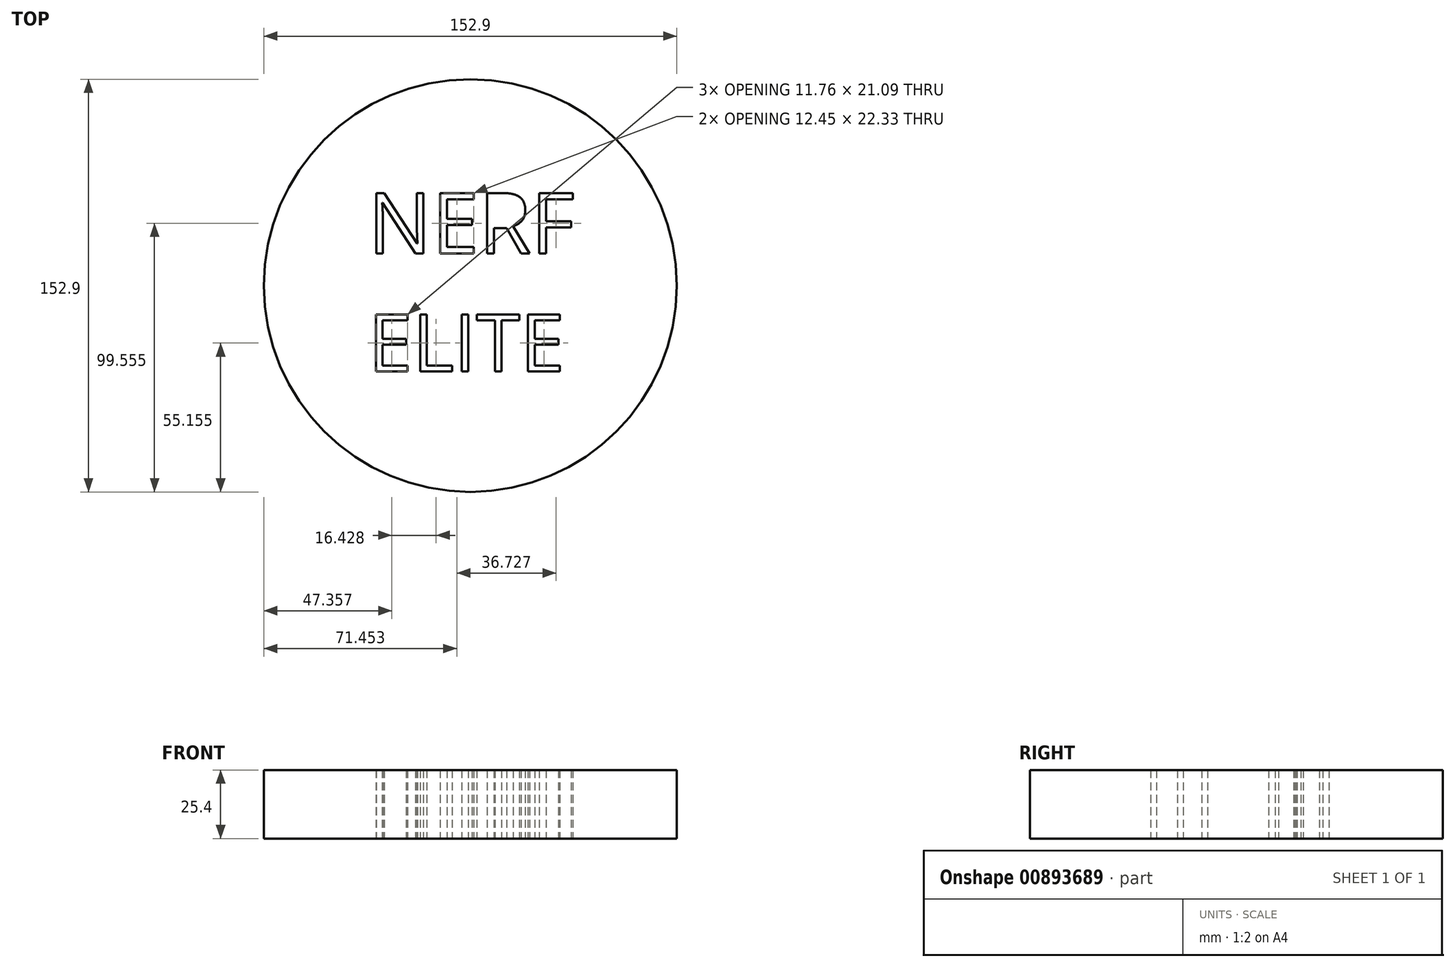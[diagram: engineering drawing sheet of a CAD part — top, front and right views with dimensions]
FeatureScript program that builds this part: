
annotation { "Feature Type Name" : "Feature", "Feature Type Description" : "" }
export const myFeature = defineFeature(function(context is Context, id is Id, definition is map)
    precondition{}
    {
        {
            var Q0;
            Q0=qCreatedBy(makeId("Top.planeOp"),FACE);
            var sketch = newSketch(context, id + "F0", { "sketchPlane" : qUnion([Q0])});
            skCircle(sketch, "E0", {"center": v(0, 0) * mm, "radius": 76.45 * mm});
            skPoint(sketch, "E1.start.orphan", {"position": v(-19, 61) * mm});
            skPoint(sketch, "E2.end.orphan", {"position": v(0, 66.3) * mm});
            skPoint(sketch, "E3.orphan", {"position": v(-6.7, 66.3) * mm});
            skPoint(sketch, "E4.orphan", {"position": v(-6.7, 61.38) * mm});
            skPoint(sketch, "E5.end.orphan", {"position": v(0, 55.7) * mm});
            skPoint(sketch, "E6.start.orphan", {"position": v(0, 61.38) * mm});
            skPoint(sketch, "E7.start.orphan", {"position": v(7.77, 66.3) * mm});
            skPoint(sketch, "E8.end.orphan", {"position": v(7.77, 55.7) * mm});
            skPoint(sketch, "E8.start.orphan", {"position": v(7.77, 61.38) * mm});
            skLineSegment(sketch, "E9", {"start": v(2.86, 56.23) * mm, "end": v(2.87, 56.23) * mm});
            skPoint(sketch, "E10.start.orphan", {"position": v(-1.19, 62.03) * mm});
            skText(sketch, "E11", { "text": "NERF\n", "fontName": "OpenSans-Regular.ttf"});
            skPoint(sketch, "E12.start.orphan", {"position": v(-30.54, 66.3) * mm});
            skPoint(sketch, "E13.start.orphan", {"position": v(-30.54, 68.75) * mm});
            skPoint(sketch, "E14.end.orphan", {"position": v(-24.08, 66.3) * mm});
            skPoint(sketch, "E15.start.orphan", {"position": v(-21.53, 68.75) * mm});
            skPoint(sketch, "E16.start.orphan", {"position": v(-13.15, 68.75) * mm});
            skPoint(sketch, "E17.end.orphan", {"position": v(-13.15, 66.3) * mm});
            skPoint(sketch, "E18.end.orphan", {"position": v(-19, 66.3) * mm});
            skPoint(sketch, "E19.end.orphan", {"position": v(-19, 61.65) * mm});
            skPoint(sketch, "E20.start.orphan", {"position": v(-19, 55.7) * mm});
            skPoint(sketch, "E21.start.orphan", {"position": v(-13.15, 55.7) * mm});
            skPoint(sketch, "E22.end.orphan", {"position": v(-1.12, 66.3) * mm});
            skPoint(sketch, "E23.end.orphan", {"position": v(-4.41, 64) * mm});
            skPoint(sketch, "E23.start.orphan", {"position": v(-4.41, 66.3) * mm});
            skPoint(sketch, "E24.end.orphan", {"position": v(1.65, 62.03) * mm});
            skPoint(sketch, "E25.end.orphan", {"position": v(-4.02, 55.7) * mm});
            skPoint(sketch, "E25.start.orphan", {"position": v(-4.02, 62.03) * mm});
            skPoint(sketch, "E26.end.orphan", {"position": v(-4.68, 55.7) * mm});
            skPoint(sketch, "E26.start.orphan", {"position": v(-6.7, 55.7) * mm});
            skPoint(sketch, "E27.end.orphan", {"position": v(9.81, 70.33) * mm});
            skPoint(sketch, "E28.start.orphan", {"position": v(17.58, 68.09) * mm});
            skPoint(sketch, "E29.start.orphan", {"position": v(13.9, 66.3) * mm});
            skPoint(sketch, "E30.end.orphan", {"position": v(17.58, 64) * mm});
            skPoint(sketch, "E31.end.orphan", {"position": v(17.58, 62.03) * mm});
            skPoint(sketch, "E32.end.orphan", {"position": v(13.9, 64.67) * mm});
            skPoint(sketch, "E33.end.orphan", {"position": v(13.9, 62.03) * mm});
            skPoint(sketch, "E34.end.orphan", {"position": v(13.9, 56.23) * mm});
            skPoint(sketch, "E34.start.orphan", {"position": v(9.81, 56.23) * mm});
            skLineSegment(sketch, "E35", {"start": v(-27.85, -42.67) * mm, "end": v(-27.85, -55.58) * mm});
            skLineSegment(sketch, "E36", {"start": v(-27.46, -55.58) * mm, "end": v(-22.06, -51.23) * mm});
            skLineSegment(sketch, "E37", {"start": v(-22.06, -51.23) * mm, "end": v(-22.06, -42.8) * mm});
            skLineSegment(sketch, "E38", {"start": v(-22.72, -42.8) * mm, "end": v(-27.85, -42.67) * mm});
            skLineSegment(sketch, "E39", {"start": v(-22.06, -51.23) * mm, "end": v(-15.5, -45.96) * mm});
            skLineSegment(sketch, "E40", {"start": v(-21.14, -42.8) * mm, "end": v(-18.37, -42.8) * mm});
            skLineSegment(sketch, "E41", {"start": v(-18.37, -42.54) * mm, "end": v(-18.37, -37.93) * mm});
            skLineSegment(sketch, "E42", {"start": v(-18.37, -37.93) * mm, "end": v(-12.05, -37.93) * mm});
            skArc(sketch, "E43", {"start": v(-8.89, -45.96) * mm, "mid": v(-12.2, -44.79) * mm, "end": v(-15.5, -45.96) * mm});
            skLineSegment(sketch, "E44", {"start": v(-8.89, -45.96) * mm, "end": v(-11.4, -52.68) * mm});
            skLineSegment(sketch, "E45", {"start": v(-11.4, -52.68) * mm, "end": v(-6.39, -52.68) * mm});
            skLineSegment(sketch, "E46", {"start": v(-6.39, -53.08) * mm, "end": v(-5.33, -45.96) * mm});
            skArc(sketch, "E47", {"start": v(1.25, -45.96) * mm, "mid": v(-2.04, -44.7) * mm, "end": v(-5.33, -45.96) * mm});
            skLineSegment(sketch, "E48", {"start": v(1.25, -45.96) * mm, "end": v(8.89, -45.96) * mm});
            skLineSegment(sketch, "E49", {"start": v(8.89, -45.96) * mm, "end": v(8.89, -61.9) * mm});
            skLineSegment(sketch, "E50", {"start": v(8.89, -61.9) * mm, "end": v(14.55, -61.9) * mm});
            skLineSegment(sketch, "E51", {"start": v(14.55, -61.9) * mm, "end": v(14.55, -45.96) * mm});
            skLineSegment(sketch, "E52", {"start": v(14.55, -45.96) * mm, "end": v(19.95, -45.96) * mm});
            skLineSegment(sketch, "E53", {"start": v(19.95, -45.17) * mm, "end": v(19.95, -43.6) * mm});
            skLineSegment(sketch, "E54", {"start": v(19.95, -43.6) * mm, "end": v(22.06, -43.6) * mm});
            skLineSegment(sketch, "E55", {"start": v(22.06, -43.6) * mm, "end": v(22.06, -41.49) * mm});
            skLineSegment(sketch, "E56", {"start": v(22.06, -41.49) * mm, "end": v(29.3, -41.49) * mm});
            skLineSegment(sketch, "E57", {"start": v(29.3, -41.49) * mm, "end": v(29.3, -43.6) * mm});
            skLineSegment(sketch, "E58", {"start": v(29.3, -43.6) * mm, "end": v(31.41, -43.6) * mm});
            skLineSegment(sketch, "E59", {"start": v(31.41, -43.6) * mm, "end": v(31.41, -46.62) * mm});
            skLineSegment(sketch, "E60", {"start": v(31.41, -46.62) * mm, "end": v(31.41, -48.73) * mm});
            skLineSegment(sketch, "E61", {"start": v(31.41, -48.73) * mm, "end": v(33.65, -48.73) * mm});
            skLineSegment(sketch, "E62", {"start": v(33.65, -48.73) * mm, "end": v(33.65, -43.6) * mm});
            skLineSegment(sketch, "E63", {"start": v(33.65, -43.6) * mm, "end": v(35.89, -43.6) * mm});
            skLineSegment(sketch, "E64", {"start": v(35.89, -43.6) * mm, "end": v(35.89, -41.49) * mm});
            skLineSegment(sketch, "E65", {"start": v(35.89, -41.49) * mm, "end": v(38.92, -41.49) * mm});
            skLineSegment(sketch, "E66", {"start": v(38.92, -41.49) * mm, "end": v(38.92, -37.14) * mm});
            skLineSegment(sketch, "E67", {"start": v(38.92, -37.14) * mm, "end": v(-12.05, -37.93) * mm});
            skLineSegment(sketch, "E68", {"start": v(19.7, -37.44) * mm, "end": v(19.68, -36.22) * mm});
            skLineSegment(sketch, "E69", {"start": v(34.18, -36) * mm, "end": v(34.2, -37.21) * mm});
            skLineSegment(sketch, "E70", {"start": v(16.67, -37.48) * mm, "end": v(16.65, -36.36) * mm});
            skLineSegment(sketch, "E71", {"start": v(16.65, -36.36) * mm, "end": v(7.84, -36.5) * mm});
            skLineSegment(sketch, "E72", {"start": v(7.84, -36.5) * mm, "end": v(7.84, -37.48) * mm});
            skArc(sketch, "E73", {"start": v(-18.37, -37.93) * mm, "mid": v(-20.68, -40.23) * mm, "end": v(-18.37, -42.54) * mm});
            skLineSegment(sketch, "E74", {"start": v(-21.14, -42.8) * mm, "end": v(-22.06, -42.8) * mm});
            skText(sketch, "E75", { "text": "ELITE", "fontName": "OpenSans-Regular.ttf"});
            const initialGuessF0  = {"E11": [-0.03787, 0.01194, 1, 0, 0.02252], "E75": [-0.03787, -0.03184, 1, 0, 0.02127]};
            skSetInitialGuess(sketch, initialGuessF0);
            skSolve(sketch);
        }
        {
            var Q0;
            {var subQ3=sQuery(id+"F0.wireOp",EDGE,"E2");Q0=makeQuery(id+"F0.imprint","IMPRINT",FACE,{"disambiguationData":[TD([[makeQuery(id+"F0.imprint","IMPRINT",EDGE,{"derivedFrom":subQ3}),-1.0]])]});}
            var Q1;
            Q1=makeQuery(id+"F0.imprint","IMPRINT",FACE,{"disambiguationData":[TD([[makeQuery(id+"F0.imprint","IMPRINT",EDGE,{"derivedFrom":sQuery(id+"F0.wireOp",EDGE,"E41")}),1.0]])]});
            var Q2;
            Q2=makeQuery(id+"F0.imprint","IMPRINT",FACE,{"disambiguationData":[TD([[makeQuery(id+"F0.imprint","IMPRINT",EDGE,{"derivedFrom":sQuery(id+"F0.wireOp",EDGE,"E0")}),1.0]])]});
            extrude(context, id + "F1", {"entities" : qUnion([Q0, Q1, Q2]), "depth" : 25.4 * mm, "offsetDistance" : 25.4 * mm});
        }
    });
